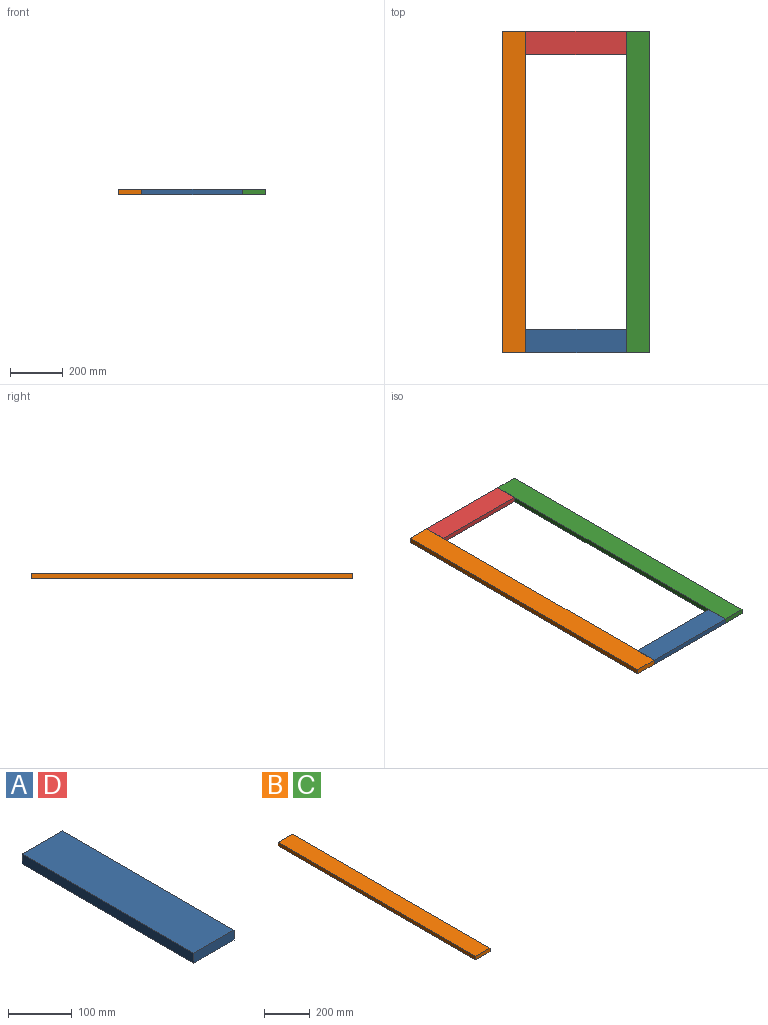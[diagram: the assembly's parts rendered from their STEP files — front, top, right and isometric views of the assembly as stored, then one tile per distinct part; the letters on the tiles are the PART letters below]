
ASSEMBLY  parts=4 mates=9
PART A: 6 faces, bbox 88.9x381x19.1 mm
  f0: plane 381x19.05mm, normal (1,0,0), area 7258mm2, adj f1,f3,f4,f5
  f1: plane 381x88.9mm, normal (0,0,1), area 33870.9mm2, adj f0,f2,f4,f5
  f2: plane 381x19.05mm, normal (-1,0,0), area 7258mm2, adj f1,f3,f4,f5
  f3: plane 381x88.9mm, normal (0,0,-1), area 33870.9mm2, adj f0,f2,f4,f5
  f4: plane 88.9x19.05mm, normal (0,-1,0), area 1693.5mm2, adj f0,f1,f2,f3
  f5: plane 88.9x19.05mm, normal (0,1,0), area 1693.5mm2, adj f0,f1,f2,f3
PART B: 6 faces, bbox 88.9x1219.2x19.1 mm
  f0: plane 1219.2x19.05mm, normal (1,0,0), area 23225.8mm2, adj f1,f3,f4,f5
  f1: plane 1219.2x88.9mm, normal (0,0,1), area 108386.9mm2, adj f0,f2,f4,f5
  f2: plane 1219.2x19.05mm, normal (-1,0,0), area 23225.8mm2, adj f1,f3,f4,f5
  f3: plane 1219.2x88.9mm, normal (0,0,-1), area 108386.9mm2, adj f0,f2,f4,f5
  f4: plane 88.9x19.05mm, normal (0,-1,0), area 1693.5mm2, adj f0,f1,f2,f3
  f5: plane 88.9x19.05mm, normal (0,1,0), area 1693.5mm2, adj f0,f1,f2,f3
PART C: same geometry as B
PART D: same geometry as A
PLACE A rot(axis=(0,0,-1),90deg) t=(-491.12,-892.77,-119.01)mm
PLACE B t=(-916.57,281.98,-119.01)mm
PLACE C t=(-446.67,281.98,-119.01)mm
PLACE D rot(axis=(0,0,1),90deg) t=(-872.12,237.53,-119.01)mm
MATE planar A.f4 <-> B.f0  axis (-1,0,0) through (-872.12,-892.77,-119.01)mm
MATE planar C.f4 <-> A.f0  axis (0,-1,0) through (-446.67,-937.22,-119.01)mm
MATE planar A.f5 <-> C.f2  axis (1,0,0) through (-491.12,-892.77,-119.01)mm
MATE planar A.f0 <-> B.f4  axis (0,-1,0) through (-681.62,-937.22,-119.01)mm
MATE planar B.f1 <-> C.f1  axis (0,0,1) through (-916.57,-327.62,-109.48)mm
MATE planar B.f1 <-> D.f1  axis (0,0,1) through (-916.57,-327.62,-109.48)mm
MATE planar D.f4 <-> C.f2  axis (1,0,0) through (-491.12,237.53,-119.01)mm
MATE planar B.f1 <-> A.f1  axis (0,0,1) through (-916.57,-327.62,-109.48)mm
MATE planar C.f5 <-> D.f0  axis (0,1,0) through (-446.67,281.98,-119.01)mm
